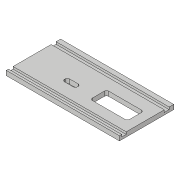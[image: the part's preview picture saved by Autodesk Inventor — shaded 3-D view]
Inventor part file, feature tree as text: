
AUTODESK INVENTOR PART (.ipt)
format: ipt  version: 2018.3 (Build 223284000, 284)  size: 135,680 bytes
history: native  units: in
note: dims shown in document units (in); Inventor stores cm internally (conversion verified against a paired STEP export)
features: extrude x3, sketch x3, fillet x2
ambient origin geometry x8: Origin, YZ Plane, XZ Plane, XY Plane, X Axis, Y Axis, Z Axis, Center Point
bodies: Solid1 (feature_tree)
feature tree (8):
  extrude  "Extrusion1"  Depth=1.5in
  extrude  "Extrusion2"  Depth=0.126in
  extrude  "Extrusion4"  Depth=0.0625in
  fillet  "Fillet1"  Radius=0.125in
  fillet  "Fillet2"  Radius=0.135in
  sketch  "Sketch1"  dims[d0=3.125in d1=1.5in]
  sketch  "Sketch2"  dims[d2=0.125in d3=0.0in d4=0.126in]
  sketch  "Sketch4"  dims[d6=0.0625in d7=0.0in d8=0.0625in d13=0.125in d14=0.135in d15=0.14in d16=0.36in d17=0.3425in d18=1.75in d19=1.025in d20=0.45in d21=0.28in d22=0.25in d23=1.0in d24=0.0in d25=0.0625in d26=0.0625in]
